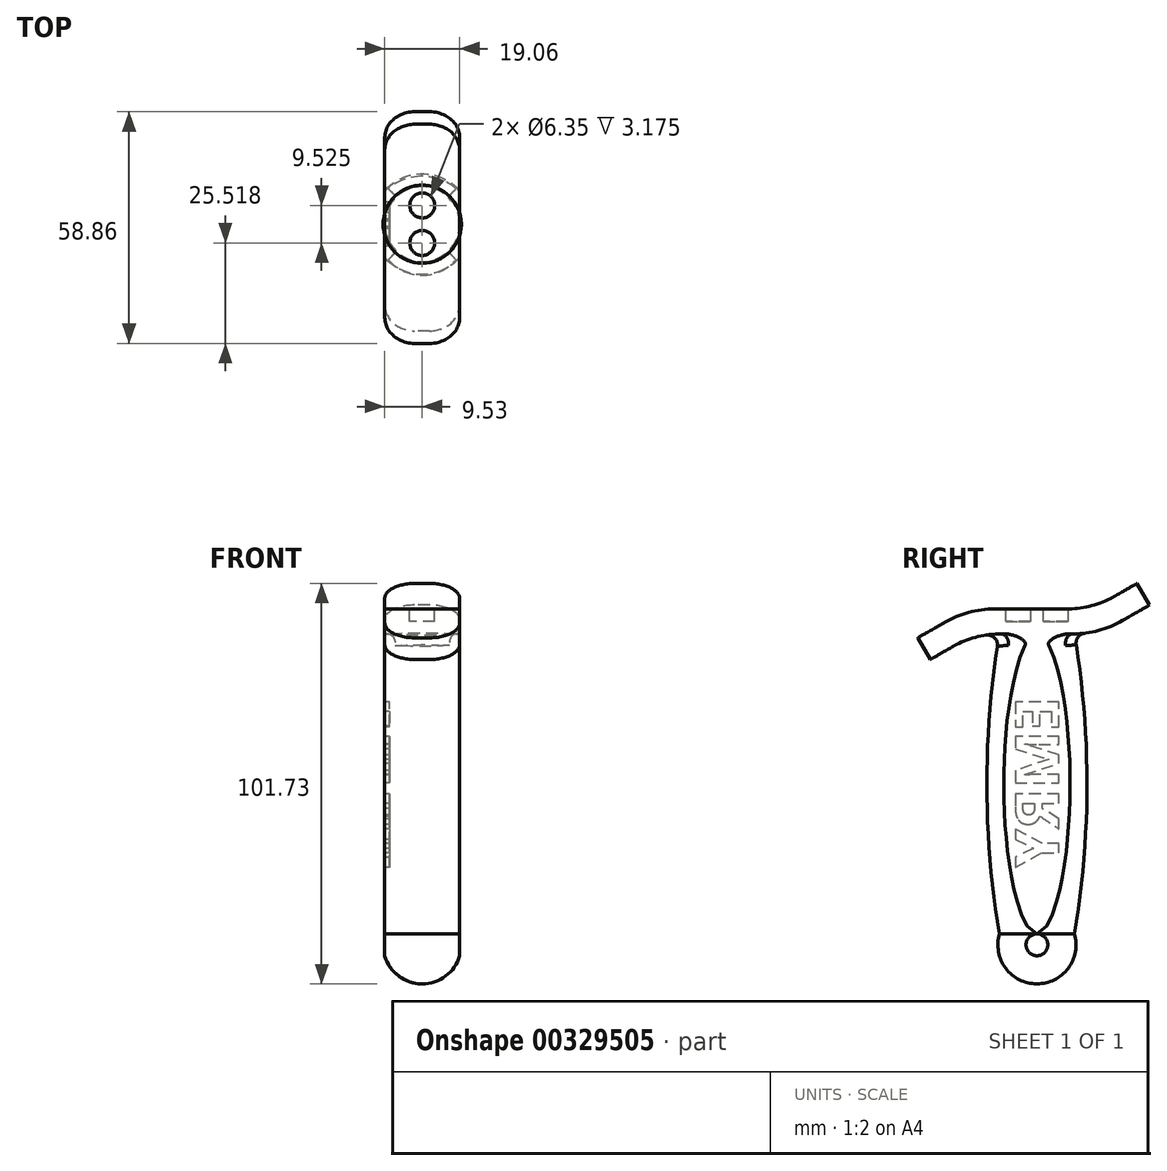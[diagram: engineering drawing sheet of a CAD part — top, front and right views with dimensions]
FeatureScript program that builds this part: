
annotation { "Feature Type Name" : "Feature", "Feature Type Description" : "" }
export const myFeature = defineFeature(function(context is Context, id is Id, definition is map)
    precondition{}
    {
        {
            var Q0;
            Q0=qCreatedBy(makeId("Front.planeOp"),FACE);
            var sketch = newSketch(context, id + "F0", { "sketchPlane" : qUnion([Q0])});
            skLineSegment(sketch, "E0", {"start": v(0, 38.1) * mm, "end": v(0, -38.1) * mm});
            skArc(sketch, "E1", {"start": v(-9.53, 38.1) * mm, "mid": v(-12.72, 0) * mm, "end": v(-9.53, -38.1) * mm});
            skLineSegment(sketch, "E2", {"start": v(-9.53, 38.1) * mm, "end": v(0, 38.1) * mm});
            skLineSegment(sketch, "E3", {"start": v(0, -38.1) * mm, "end": v(-9.53, -38.1) * mm});
            skSolve(sketch);
        }
        {
            var Q0;
            Q0 = qSketchRegion(id + "F0", true);
            var Q1;
            Q1 = qConstructionFilter(qBodyType(qCreatedBy(id + "F0" ,EDGE), BodyType.WIRE), ConstructionObject.NO);
            var Q2;
            Q2=sQuery(id+"F0.wireOp",EDGE,"E0");
            revolve(context, id + "F1", {"entities" : qUnion([Q0]), "surfaceEntities" : qUnion([Q1]), "axis" : qUnion([Q2]), "revolveType" : RevolveType.FULL});
        }
        {
            var Q0;
            Q0=qCreatedBy(makeId("Front.planeOp"),FACE);
            var sketch = newSketch(context, id + "F2", { "sketchPlane" : qUnion([Q0])});
            skLineSegment(sketch, "E4", {"start": v(0, -38.1) * mm, "end": v(-9.53, -38.1) * mm});
            skLineSegment(sketch, "E5", {"start": v(0, -38.1) * mm, "end": v(0, -50.8) * mm});
            skLineSegment(sketch, "E6", {"start": v(0, -50.8) * mm, "end": v(13.1, -50.8) * mm, "construction": true});
            skArc(sketch, "E7", {"start": v(-9.53, -38.1) * mm, "mid": v(-7.94, -46.83) * mm, "end": v(0, -50.8) * mm});
            skSolve(sketch);
        }
        {
            var Q0;
            Q0 = qSketchRegion(id + "F2", true);
            var Q1;
            Q1=sQuery(id+"F2.wireOp",EDGE,"E5");
            revolve(context, id + "F3", {"operationType" : NewBodyOperationType.ADD, "entities" : qUnion([Q0]), "axis" : qUnion([Q1]), "revolveType" : RevolveType.FULL});
        }
        {
            var Q0;
            Q0=makeQuery(id+"F1.opRevolve","SWEPT_FACE",FACE,{"disambiguationData":[OSD([sQuery(id+"F0.wireOp",EDGE,"E2")])]});
            var sketch = newSketch(context, id + "F4", { "sketchPlane" : qUnion([Q0])});
            skLineSegment(sketch, "E8.bottom", {"start": v(-15.87, 16.08) * mm, "end": v(-9.53, 16.08) * mm});
            skLineSegment(sketch, "E8.top", {"start": v(-15.87, -16.08) * mm, "end": v(-9.53, -16.08) * mm});
            skLineSegment(sketch, "E8.left", {"start": v(-15.87, 16.08) * mm, "end": v(-15.88, -16.08) * mm});
            skLineSegment(sketch, "E8.right", {"start": v(-9.53, 16.08) * mm, "end": v(-9.52, -16.08) * mm});
            skLineSegment(sketch, "E9.bottom", {"start": v(9.53, 26.21) * mm, "end": v(15.88, 26.21) * mm});
            skLineSegment(sketch, "E9.top", {"start": v(9.53, -26.21) * mm, "end": v(15.88, -26.21) * mm});
            skLineSegment(sketch, "E9.left", {"start": v(9.53, 26.21) * mm, "end": v(9.53, -26.21) * mm});
            skLineSegment(sketch, "E9.right", {"start": v(15.87, 26.21) * mm, "end": v(15.88, -26.21) * mm});
            skLineSegment(sketch, "E10", {"start": v(-9.53, 0) * mm, "end": v(9.53, 0) * mm});
            skSolve(sketch);
        }
        {
            var Q0;
            {var subQ1=sQuery(id+"F4.wireOp",EDGE,"E8.bottom");Q0=makeQuery(id+"F4.imprint","IMPRINT",FACE,{"disambiguationData":[TD([[makeQuery(id+"F4.imprint","IMPRINT",EDGE,{"derivedFrom":subQ1}),-1.0]])]});}
            var Q1;
            {var subQ3=sQuery(id+"F4.wireOp",EDGE,"E9.bottom");Q1=makeQuery(id+"F4.imprint","IMPRINT",FACE,{"disambiguationData":[TD([[makeQuery(id+"F4.imprint","IMPRINT",EDGE,{"derivedFrom":subQ3}),-1.0]])]});}
            extrude(context, id + "F5", {"entities" : qUnion([Q0, Q1]), "operationType" : NewBodyOperationType.REMOVE, "endBound" : BoundingType.THROUGH_ALL, "oppositeDirection" : true, "depth" : 25.4 * mm});
        }
        {
            var Q0;
            {var subQ0=makeQuery(id+"F5.opExtrude","SWEPT_FACE",FACE,{"disambiguationData":[OSD([sQuery(id+"F4.wireOp",EDGE,"E8.right")])]});Q0=makeQuery(id+"F5.boolean.opBoolean","COPY",FACE,{"disambiguationData":[TD([makeQuery(id+"F1.opRevolve","SWEPT_FACE",FACE,{"disambiguationData":[OSD([sQuery(id+"F0.wireOp",EDGE,"E1")])]}),makeQuery(id+"F1.opRevolve","SWEPT_FACE",FACE,{"disambiguationData":[OSD([sQuery(id+"F0.wireOp",EDGE,"E2")])]}),makeQuery(id+"F3.opRevolve","SWEPT_FACE",FACE,{"disambiguationData":[OSD([sQuery(id+"F2.wireOp",EDGE,"E7")])]}),subQ0])],"derivedFrom":subQ0});}
            var sketch = newSketch(context, id + "F6", { "sketchPlane" : qUnion([Q0])});
            skText(sketch, "E11", { "text": "EMRY", "fontName": "OpenSans-Bold.ttf"});
            const initialGuessF6  = {"E11": [-0.00561, 0.02223, 0, -1, 0.01122]};
            skSetInitialGuess(sketch, initialGuessF6);
            skSolve(sketch);
        }
        {
            var Q0;
            Q0 = qSketchRegion(id + "F6", true);
            extrude(context, id + "F7", {"entities" : qUnion([Q0]), "operationType" : NewBodyOperationType.REMOVE, "oppositeDirection" : true, "depth" : 1.27 * mm});
        }
        {
            var Q0;
            {var subQ0=makeQuery(id+"F1.opRevolve","SWEPT_FACE",FACE,{"disambiguationData":[OSD([sQuery(id+"F0.wireOp",EDGE,"E2")])]});var subQ1=makeQuery(id+"F1.opRevolve","SWEPT_FACE",FACE,{"disambiguationData":[OSD([sQuery(id+"F0.wireOp",EDGE,"E1")])]});var subQ2=makeQuery(id+"F3.opRevolve","SWEPT_FACE",FACE,{"disambiguationData":[OSD([sQuery(id+"F2.wireOp",EDGE,"E7")])]});var subQ3=makeQuery(id+"F5.opExtrude","SWEPT_FACE",FACE,{"disambiguationData":[OSD([sQuery(id+"F4.wireOp",EDGE,"E8.right")])]});Q0=makeQuery(id+"F7.boolean.opBoolean","SPLIT",FACE,{"disambiguationData":[TD([subQ1])],"derivedFrom":makeQuery(id+"F5.boolean.opBoolean","COPY",FACE,{"disambiguationData":[TD([subQ1,subQ0,subQ2,subQ3])],"derivedFrom":subQ3})});}
            var sketch = newSketch(context, id + "F8", { "sketchPlane" : qUnion([Q0])});
            skLineSegment(sketch, "E12.bottom", {"start": v(-7.37, 44.45) * mm, "end": v(10.77, 44.45) * mm});
            skLineSegment(sketch, "E12.top", {"start": v(-9.07, 38.1) * mm, "end": v(9.07, 38.1) * mm});
            skLineSegment(sketch, "E13", {"start": v(-21.77, 41.5) * mm, "end": v(-28.57, 45.43) * mm});
            skLineSegment(sketch, "E14", {"start": v(-28.57, 45.43) * mm, "end": v(-25.4, 50.93) * mm});
            skLineSegment(sketch, "E15", {"start": v(-25.4, 50.93) * mm, "end": v(-20.07, 47.85) * mm});
            skLineSegment(sketch, "E16", {"start": v(23.47, 41.05) * mm, "end": v(30.28, 37.12) * mm});
            skLineSegment(sketch, "E17", {"start": v(30.28, 37.12) * mm, "end": v(27.1, 31.62) * mm});
            skLineSegment(sketch, "E18", {"start": v(27.1, 31.62) * mm, "end": v(21.77, 34.7) * mm});
            skPoint(sketch, "E19.visualSharp", {"position": v(-14.17, 44.45) * mm});
            skArc(sketch, "E19.filletArc", {"start": v(-20.07, 47.85) * mm, "mid": v(-13.94, 45.32) * mm, "end": v(-7.37, 44.45) * mm});
            skPoint(sketch, "E20.visualSharp", {"position": v(-15.88, 38.1) * mm});
            skArc(sketch, "E20.filletArc", {"start": v(-21.77, 41.5) * mm, "mid": v(-15.64, 38.97) * mm, "end": v(-9.07, 38.1) * mm});
            skPoint(sketch, "E21.visualSharp", {"position": v(17.58, 44.45) * mm});
            skArc(sketch, "E21.filletArc", {"start": v(23.47, 41.05) * mm, "mid": v(17.34, 43.58) * mm, "end": v(10.77, 44.45) * mm});
            skPoint(sketch, "E22.visualSharp", {"position": v(15.88, 38.1) * mm});
            skArc(sketch, "E22.filletArc", {"start": v(21.77, 34.7) * mm, "mid": v(15.64, 37.23) * mm, "end": v(9.07, 38.1) * mm});
            skSolve(sketch);
        }
        {
            var Q0;
            Q0=makeQuery(id+"F8.imprint","IMPRINT",FACE,{"disambiguationData":[TD([[makeQuery(id+"F8.imprint","IMPRINT",EDGE,{"derivedFrom":sQuery(id+"F8.wireOp",EDGE,"E12.bottom")}),-1.0]])]});
            var Q1;
            {var subQ0=makeQuery(id+"F5.opExtrude","SWEPT_FACE",FACE,{"disambiguationData":[OSD([sQuery(id+"F4.wireOp",EDGE,"E9.left")])]});Q1=makeQuery(id+"F5.boolean.opBoolean","COPY",FACE,{"disambiguationData":[TD([makeQuery(id+"F1.opRevolve","SWEPT_FACE",FACE,{"disambiguationData":[OSD([sQuery(id+"F0.wireOp",EDGE,"E1")])]}),makeQuery(id+"F1.opRevolve","SWEPT_FACE",FACE,{"disambiguationData":[OSD([sQuery(id+"F0.wireOp",EDGE,"E2")])]}),makeQuery(id+"F3.opRevolve","SWEPT_FACE",FACE,{"disambiguationData":[OSD([sQuery(id+"F2.wireOp",EDGE,"E7")])]}),subQ0])],"derivedFrom":subQ0});}
            extrude(context, id + "F9", {"entities" : qUnion([Q0]), "operationType" : NewBodyOperationType.ADD, "endBound" : BoundingType.UP_TO_SURFACE, "oppositeDirection" : true, "endBoundEntityFace" : qUnion([Q1]), "depth" : 25.4 * mm});
        }
        {
            var Q0;
            Q0=makeQuery(id+"F9.opExtrude","CAP_EDGE",EDGE,{"disambiguationData":[OSD([sQuery(id+"F8.wireOp",EDGE,"E14")])],"isStart":true});
            var Q1;
            Q1=makeQuery(id+"F9.opExtrude","CAP_EDGE",EDGE,{"disambiguationData":[OSD([sQuery(id+"F8.wireOp",EDGE,"E14")])],"isStart":false});
            var Q2;
            Q2=makeQuery(id+"F9.opExtrude","CAP_EDGE",EDGE,{"disambiguationData":[OSD([sQuery(id+"F8.wireOp",EDGE,"E17")])],"isStart":true});
            var Q3;
            Q3=makeQuery(id+"F9.opExtrude","CAP_EDGE",EDGE,{"disambiguationData":[OSD([sQuery(id+"F8.wireOp",EDGE,"E17")])],"isStart":false});
            fillet(context, id + "F10", {"entities" : qUnion([Q0, Q1, Q2, Q3]), "radius" : 7.62 * mm, "tangentPropagation" : true, "allowEdgeOverflow" : false});
        }
        {
            var Q0;
            {var subQ0=sQuery(id+"F8.wireOp",EDGE,"E12.top");var subQ1=makeQuery(id+"F9.opExtrude","SWEPT_FACE",FACE,{"disambiguationData":[OSD([subQ0])]});var subQ3=sQuery(id+"F0.wireOp",EDGE,"E1");var subQ4=makeQuery(id+"F1.opRevolve","SWEPT_FACE",FACE,{"disambiguationData":[OSD([subQ3])]});var subQ5=sQuery(id+"F0.wireOp",EDGE,"E2");var subQ6=makeQuery(id+"F5.opExtrude","SWEPT_FACE",FACE,{"disambiguationData":[OSD([sQuery(id+"F4.wireOp",EDGE,"E9.left")])]});Q0=makeQuery(id+"F9.boolean.opBoolean","SPLIT",EDGE,{"disambiguationData":[topologyDisambiguationEdgeConnected([subQ4,subQ1]),TD([makeQuery(id+"F5.boolean.opBoolean","COPY",FACE,{"disambiguationData":[TD([subQ4,makeQuery(id+"F1.opRevolve","SWEPT_FACE",FACE,{"disambiguationData":[OSD([subQ5])]}),makeQuery(id+"F3.opRevolve","SWEPT_FACE",FACE,{"disambiguationData":[OSD([sQuery(id+"F2.wireOp",EDGE,"E7")])]}),subQ6])],"derivedFrom":subQ6})])],"derivedFrom":makeQuery(id+"F5.boolean.opBoolean","SPLIT",EDGE,{"disambiguationData":[OD(0.0)],"derivedFrom":makeQuery(id+"F1.opRevolve","SWEPT_EDGE",EDGE,{"disambiguationData":[OSD([subQ3,subQ5])]})})});}
            var Q1;
            {var subQ0=sQuery(id+"F8.wireOp",EDGE,"E12.top");var subQ1=makeQuery(id+"F9.opExtrude","SWEPT_FACE",FACE,{"disambiguationData":[OSD([subQ0])]});var subQ3=sQuery(id+"F0.wireOp",EDGE,"E1");var subQ4=makeQuery(id+"F1.opRevolve","SWEPT_FACE",FACE,{"disambiguationData":[OSD([subQ3])]});var subQ5=sQuery(id+"F0.wireOp",EDGE,"E2");var subQ6=makeQuery(id+"F5.opExtrude","SWEPT_FACE",FACE,{"disambiguationData":[OSD([sQuery(id+"F4.wireOp",EDGE,"E9.left")])]});Q1=makeQuery(id+"F9.boolean.opBoolean","SPLIT",EDGE,{"disambiguationData":[topologyDisambiguationEdgeConnected([subQ4,subQ1]),TD([makeQuery(id+"F5.boolean.opBoolean","COPY",FACE,{"disambiguationData":[TD([subQ4,makeQuery(id+"F1.opRevolve","SWEPT_FACE",FACE,{"disambiguationData":[OSD([subQ5])]}),makeQuery(id+"F3.opRevolve","SWEPT_FACE",FACE,{"disambiguationData":[OSD([sQuery(id+"F2.wireOp",EDGE,"E7")])]}),subQ6])],"derivedFrom":subQ6})])],"derivedFrom":makeQuery(id+"F5.boolean.opBoolean","SPLIT",EDGE,{"disambiguationData":[OD(1.0)],"derivedFrom":makeQuery(id+"F1.opRevolve","SWEPT_EDGE",EDGE,{"disambiguationData":[OSD([subQ3,subQ5])]})})});}
            fillet(context, id + "F11", {"entities" : qUnion([Q0, Q1]), "radius" : 2.54 * mm, "tangentPropagation" : true, "allowEdgeOverflow" : false});
        }
        {
            var Q0;
            Q0=makeQuery(id+"F9.opExtrude","SWEPT_FACE",FACE,{"disambiguationData":[OSD([sQuery(id+"F8.wireOp",EDGE,"E12.bottom")])]});
            var sketch = newSketch(context, id + "F12", { "sketchPlane" : qUnion([Q0])});
            skCircle(sketch, "E23", {"center": v(0, -4.76) * mm, "radius": 3.18 * mm});
            skCircle(sketch, "E24", {"center": v(0, 4.76) * mm, "radius": 3.18 * mm});
            skLineSegment(sketch, "E25", {"start": v(0, 4.76) * mm, "end": v(0, -4.76) * mm, "construction": true});
            skSolve(sketch);
        }
        {
            var Q0;
            Q0 = qSketchRegion(id + "F12", true);
            extrude(context, id + "F13", {"entities" : qUnion([Q0]), "operationType" : NewBodyOperationType.REMOVE, "endBound" : BoundingType.SYMMETRIC, "oppositeDirection" : true, "depth" : 6.35 * mm});
        }
    });
